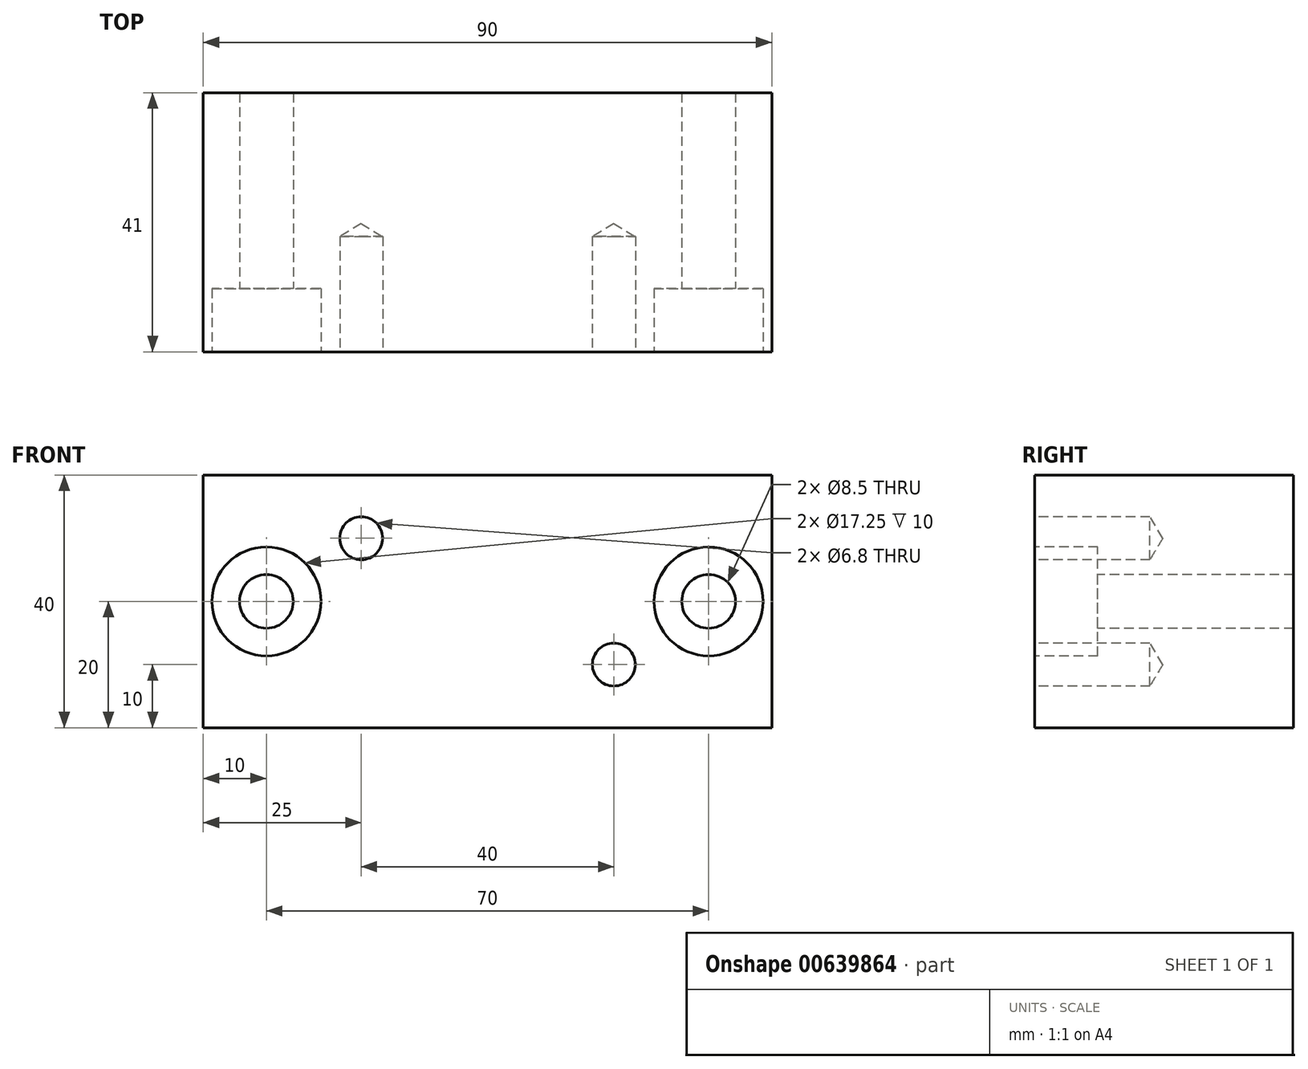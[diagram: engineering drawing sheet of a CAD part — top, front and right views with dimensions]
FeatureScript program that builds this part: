
annotation { "Feature Type Name" : "Feature", "Feature Type Description" : "" }
export const myFeature = defineFeature(function(context is Context, id is Id, definition is map)
    precondition{}
    {
        {
            var Q0;
            Q0=qCreatedBy(makeId("Front.planeOp"),FACE);
            var sketch = newSketch(context, id + "F0", { "sketchPlane" : qUnion([Q0])});
            skLineSegment(sketch, "E0.bottom", {"start": v(0, 0) * mm, "end": v(90, 0) * mm});
            skLineSegment(sketch, "E0.top", {"start": v(0, 40) * mm, "end": v(90, 40) * mm});
            skLineSegment(sketch, "E0.left", {"start": v(0, 0) * mm, "end": v(0, 40) * mm});
            skLineSegment(sketch, "E0.right", {"start": v(90, 0) * mm, "end": v(90, 40) * mm});
            skSolve(sketch);
        }
        {
            var Q0;
            Q0=makeQuery(id+"F0.imprint","IMPRINT",FACE,{"disambiguationData":[TD([[makeQuery(id+"F0.imprint","IMPRINT",EDGE,{"derivedFrom":sQuery(id+"F0.wireOp",EDGE,"E0.bottom")}),1.0]])]});
            extrude(context, id + "F1", {"entities" : qUnion([Q0]), "depth" : 41 * mm, "offsetDistance" : 25 * mm});
        }
        {
            var Q0;
            Q0=makeQuery(id+"F1.opExtrude","CAP_FACE",FACE,{"disambiguationData":[OSD([sQuery(id+"F0.wireOp",EDGE,"E0.bottom"),sQuery(id+"F0.wireOp",EDGE,"E0.top"),sQuery(id+"F0.wireOp",EDGE,"E0.left"),sQuery(id+"F0.wireOp",EDGE,"E0.right")])],"isStart":false});
            var sketch = newSketch(context, id + "F2", { "sketchPlane" : qUnion([Q0])});
            skPoint(sketch, "E1", {"position": v(10, 20) * mm});
            skPoint(sketch, "E1.positionSnap0", {"position": v(0, 20) * mm});
            skPoint(sketch, "E2", {"position": v(80, 20) * mm});
            skPoint(sketch, "E3", {"position": v(25, 30) * mm});
            skPoint(sketch, "E4", {"position": v(65, 10) * mm});
            skSolve(sketch);
        }
        {
            var Q0;
            Q0=sQuery(id+"F2.wireOp",VERTEX,"E1");
            var Q1;
            Q1=sQuery(id+"F2.wireOp",VERTEX,"E2");
            var Q2;
            Q2=makeQuery(id+"F1.opExtrude","SWEPT_BODY",BODY,{"disambiguationData":[OSD([sQuery(id+"F0.wireOp",EDGE,"E0.bottom"),sQuery(id+"F0.wireOp",EDGE,"E0.top"),sQuery(id+"F0.wireOp",EDGE,"E0.left"),sQuery(id+"F0.wireOp",EDGE,"E0.right")])]});
            hole(context, id + "F3", {"style" : HoleStyle.C_BORE, "endStyle" : HoleEndStyle.THROUGH, "standardTappedOrClearance" : lookupTablePath({ "standard" : "ISO", "engagement" : "75%", "pitch" : "1.5 mm", "size" : "M10", "type" : "Tapped" }), "standardBlindInLast" : lookupTablePath({ "standard" : "ISO", "engagement" : "75%", "pitch" : "1.5 mm", "size" : "M10", "type" : "Tapped" }), "holeDiameter" : 8.5 * mm, "cBoreDiameter" : 17.25 * mm, "cBoreDepth" : 10 * mm, "majorDiameter" : 10 * mm, "showTappedDepth" : true, "isTappedThrough" : true, "tappedDepth" : 14.5 * mm, "tapClearance" : 3, "startFromSketch" : true, "locations" : qUnion([Q0, Q1]), "scope" : qUnion([Q2])});
        }
        {
            var Q0;
            Q0=sQuery(id+"F2.wireOp",VERTEX,"E3");
            var Q1;
            Q1=sQuery(id+"F2.wireOp",VERTEX,"E4");
            var Q2;
            Q2=makeQuery(id+"F1.opExtrude","SWEPT_BODY",BODY,{"disambiguationData":[OSD([sQuery(id+"F0.wireOp",EDGE,"E0.bottom"),sQuery(id+"F0.wireOp",EDGE,"E0.top"),sQuery(id+"F0.wireOp",EDGE,"E0.left"),sQuery(id+"F0.wireOp",EDGE,"E0.right")])]});
            hole(context, id + "F4", {"style" : HoleStyle.SIMPLE, "endStyle" : HoleEndStyle.BLIND, "standardTappedOrClearance" : lookupTablePath({ "standard" : "ISO", "engagement" : "75%", "pitch" : "1.25 mm", "size" : "M8", "type" : "Tapped" }), "standardBlindInLast" : lookupTablePath({ "standard" : "ISO", "engagement" : "75%", "pitch" : "1.25 mm", "size" : "M8", "type" : "Tapped" }), "holeDiameter" : 6.8 * mm, "majorDiameter" : 8 * mm, "showTappedDepth" : true, "holeDepth" : 18.25 * mm, "isTappedThrough" : true, "tappedDepth" : 14.5 * mm, "tapClearance" : 3, "startFromSketch" : true, "locations" : qUnion([Q0, Q1]), "scope" : qUnion([Q2])});
        }
    });
